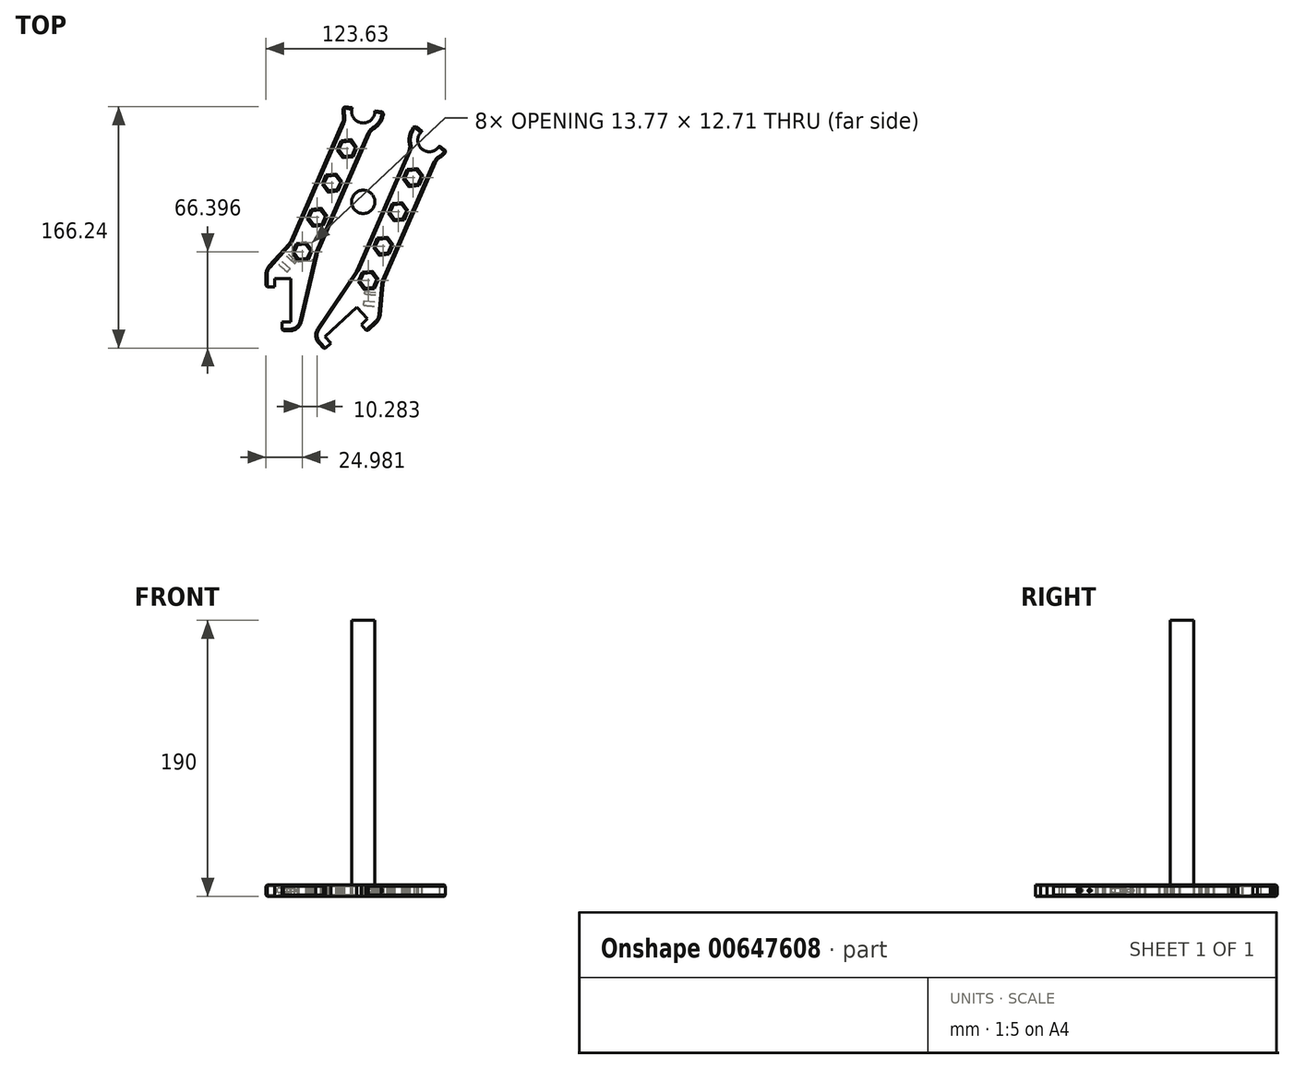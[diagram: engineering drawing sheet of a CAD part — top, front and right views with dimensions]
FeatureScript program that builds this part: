
annotation { "Feature Type Name" : "Feature", "Feature Type Description" : "" }
export const myFeature = defineFeature(function(context is Context, id is Id, definition is map)
    precondition{}
    {
        {
            var Q0;
            Q0=qCreatedBy(makeId("Top.planeOp"),FACE);
            var sketch = newSketch(context, id + "F0", { "sketchPlane" : qUnion([Q0])});
            skLineSegment(sketch, "E0.bottom", {"start": v(6, 6) * mm, "end": v(-17, 6) * mm, "construction": true});
            skLineSegment(sketch, "E0.top", {"start": v(6, -36) * mm, "end": v(-6, -36) * mm});
            skLineSegment(sketch, "E0.left", {"start": v(6, 6) * mm, "end": v(6, -36) * mm, "construction": true});
            skLineSegment(sketch, "E0.right", {"start": v(-17, 6) * mm, "end": v(-17, -6) * mm});
            skLineSegment(sketch, "E1", {"start": v(-17, -6) * mm, "end": v(-11, -6) * mm});
            skLineSegment(sketch, "E2", {"start": v(-11, -6) * mm, "end": v(-11, 0) * mm});
            skLineSegment(sketch, "E3", {"start": v(-11, 0) * mm, "end": v(0, 0) * mm});
            skLineSegment(sketch, "E4", {"start": v(0, 0) * mm, "end": v(0, -30) * mm});
            skLineSegment(sketch, "E5", {"start": v(0, -30) * mm, "end": v(-6, -30) * mm});
            skLineSegment(sketch, "E6", {"start": v(-6, -30) * mm, "end": v(-6, -36) * mm});
            skCircle(sketch, "E7", {"center": v(50, 115) * mm, "radius": 8 * mm});
            skCircle(sketch, "E8", {"center": v(50, 115) * mm, "radius": 14 * mm});
            skLineSegment(sketch, "E9", {"start": v(36.4, 118.32) * mm, "end": v(64, 114.57) * mm});
            skLineSegment(sketch, "E10", {"start": v(-17, 6) * mm, "end": v(0, 25.08) * mm});
            skLineSegment(sketch, "E11", {"start": v(0, 25.08) * mm, "end": v(36.92, 110) * mm});
            skLineSegment(sketch, "E12", {"start": v(18.34, 17.1) * mm, "end": v(6, -36) * mm});
            skLineSegment(sketch, "E13", {"start": v(18.34, 17.1) * mm, "end": v(55.26, 102.03) * mm});
            skLineSegment(sketch, "E14.0", {"start": v(0, 0) * mm, "end": v(50, 115) * mm, "construction": true});
            skLineSegment(sketch, "E15", {"start": v(0, 25.08) * mm, "end": v(18.34, 17.1) * mm, "construction": true});
            skCircle(sketch, "E16.cCircle", {"center": v(38.83, 89.3) * mm, "radius": 5.77 * mm, "construction": true});
            skLineSegment(sketch, "E16.0", {"start": v(36.53, 84.01) * mm, "end": v(33.1, 88.65) * mm});
            skLineSegment(sketch, "E16.1", {"start": v(33.1, 88.65) * mm, "end": v(35.4, 93.95) * mm});
            skLineSegment(sketch, "E16.2", {"start": v(35.4, 93.95) * mm, "end": v(41.13, 94.6) * mm});
            skLineSegment(sketch, "E16.3", {"start": v(41.13, 94.6) * mm, "end": v(44.57, 89.96) * mm});
            skLineSegment(sketch, "E16.4", {"start": v(44.57, 89.96) * mm, "end": v(42.26, 84.67) * mm});
            skLineSegment(sketch, "E16.5", {"start": v(42.26, 84.67) * mm, "end": v(36.53, 84.01) * mm});
            skCircle(sketch, "E17.cCircle", {"center": v(28.55, 65.66) * mm, "radius": 5.77 * mm, "construction": true});
            skLineSegment(sketch, "E17.0", {"start": v(26.24, 60.36) * mm, "end": v(22.81, 65) * mm});
            skLineSegment(sketch, "E17.1", {"start": v(22.81, 65) * mm, "end": v(25.11, 70.3) * mm});
            skLineSegment(sketch, "E17.2", {"start": v(25.11, 70.3) * mm, "end": v(30.85, 70.95) * mm});
            skLineSegment(sketch, "E17.3", {"start": v(30.85, 70.95) * mm, "end": v(34.28, 66.31) * mm});
            skLineSegment(sketch, "E17.4", {"start": v(34.28, 66.31) * mm, "end": v(31.98, 61.02) * mm});
            skLineSegment(sketch, "E17.5", {"start": v(31.98, 61.02) * mm, "end": v(26.24, 60.36) * mm});
            skCircle(sketch, "E18.cCircle", {"center": v(18.26, 42) * mm, "radius": 5.77 * mm, "construction": true});
            skLineSegment(sketch, "E18.0", {"start": v(15.96, 36.71) * mm, "end": v(12.53, 41.35) * mm});
            skLineSegment(sketch, "E18.1", {"start": v(12.53, 41.35) * mm, "end": v(14.83, 46.65) * mm});
            skLineSegment(sketch, "E18.2", {"start": v(14.83, 46.65) * mm, "end": v(20.57, 47.3) * mm});
            skLineSegment(sketch, "E18.3", {"start": v(20.57, 47.3) * mm, "end": v(24, 42.66) * mm});
            skLineSegment(sketch, "E18.4", {"start": v(24, 42.66) * mm, "end": v(21.7, 37.37) * mm});
            skLineSegment(sketch, "E18.5", {"start": v(21.7, 37.37) * mm, "end": v(15.96, 36.71) * mm});
            skCircle(sketch, "E19.cCircle", {"center": v(7.98, 18.36) * mm, "radius": 5.77 * mm, "construction": true});
            skLineSegment(sketch, "E19.0", {"start": v(5.68, 13.06) * mm, "end": v(2.24, 17.7) * mm});
            skLineSegment(sketch, "E19.1", {"start": v(2.24, 17.7) * mm, "end": v(4.55, 23) * mm});
            skLineSegment(sketch, "E19.2", {"start": v(4.55, 23) * mm, "end": v(10.28, 23.65) * mm});
            skLineSegment(sketch, "E19.3", {"start": v(10.28, 23.65) * mm, "end": v(13.72, 19) * mm});
            skLineSegment(sketch, "E19.4", {"start": v(13.72, 19) * mm, "end": v(11.42, 13.71) * mm});
            skLineSegment(sketch, "E19.5", {"start": v(11.42, 13.71) * mm, "end": v(5.68, 13.06) * mm});
            skLineSegment(sketch, "E20", {"start": v(41.13, 94.6) * mm, "end": v(46.81, 107.66) * mm, "construction": true});
            skLineSegment(sketch, "E21", {"start": v(30.85, 70.95) * mm, "end": v(36.53, 84.01) * mm, "construction": true});
            skLineSegment(sketch, "E22", {"start": v(20.57, 47.3) * mm, "end": v(26.24, 60.36) * mm, "construction": true});
            skLineSegment(sketch, "E23", {"start": v(10.28, 23.65) * mm, "end": v(15.96, 36.71) * mm, "construction": true});
            skLineSegment(sketch, "E24", {"start": v(5.68, 13.06) * mm, "end": v(0, 0) * mm, "construction": true});
            skSolve(sketch);
        }
        {
            var Q0;
            Q0=makeQuery(id+"F0.imprint","IMPRINT",FACE,{"disambiguationData":[TD([[makeQuery(id+"F0.imprint","IMPRINT",EDGE,{"derivedFrom":sQuery(id+"F0.wireOp",EDGE,"E0.top")}),-1.0]])]});
            var Q1;
            {var subQ0=sQuery(id+"F0.wireOp",EDGE,"E9");var subQ6=sQuery(id+"F0.wireOp",EDGE,"E7");var subQ7=makeQuery(id+"F0.imprint","INTERSECT",VERTEX,{"disambiguationData":[OD(0.0)],"derivedFrom":[subQ6,subQ0]});Q1=makeQuery(id+"F0.imprint","IMPRINT",FACE,{"disambiguationData":[TD([[makeQuery(id+"F0.imprint","IMPRINT",EDGE,{"disambiguationData":[TD([[subQ7,-1.0]])],"derivedFrom":subQ6}),-1.0]])]});}
            extrude(context, id + "F1", {"entities" : qUnion([Q0, Q1]), "depth" : 8 * mm, "offsetDistance" : 25 * mm});
        }
        {
            var Q0;
            Q0=makeQuery(id+"F1.opExtrude","SWEPT_EDGE",EDGE,{"disambiguationData":[OSD([sQuery(id+"F0.wireOp",EDGE,"E0.right"),sQuery(id+"F0.wireOp",EDGE,"E10")])]});
            var Q1;
            Q1=makeQuery(id+"F1.opExtrude","SWEPT_EDGE",EDGE,{"disambiguationData":[OSD([sQuery(id+"F0.wireOp",EDGE,"E10"),sQuery(id+"F0.wireOp",EDGE,"E11")])]});
            var Q2;
            Q2=makeQuery(id+"F1.opExtrude","SWEPT_EDGE",EDGE,{"disambiguationData":[OSD([sQuery(id+"F0.wireOp",EDGE,"E8"),sQuery(id+"F0.wireOp",EDGE,"E11")])]});
            var Q3;
            Q3=makeQuery(id+"F1.opExtrude","SWEPT_EDGE",EDGE,{"disambiguationData":[OSD([sQuery(id+"F0.wireOp",EDGE,"E8"),sQuery(id+"F0.wireOp",EDGE,"E13")])]});
            var Q4;
            Q4=makeQuery(id+"F1.opExtrude","SWEPT_EDGE",EDGE,{"disambiguationData":[OSD([sQuery(id+"F0.wireOp",EDGE,"E12"),sQuery(id+"F0.wireOp",EDGE,"E13")])]});
            var Q5;
            Q5=makeQuery(id+"F1.opExtrude","SWEPT_EDGE",EDGE,{"disambiguationData":[OSD([sQuery(id+"F0.wireOp",EDGE,"E0.top"),sQuery(id+"F0.wireOp",EDGE,"E12")])]});
            fillet(context, id + "F2", {"entities" : qUnion([Q0, Q1, Q2, Q3, Q4, Q5]), "radius" : 8 * mm, "tangentPropagation" : true, "allowEdgeOverflow" : false});
        }
        {
            var Q0;
            Q0=makeQuery(id+"F1.opExtrude","SWEPT_FACE",FACE,{"disambiguationData":[OSD([sQuery(id+"F0.wireOp",EDGE,"E10")])]});
            var sketch = newSketch(context, id + "F3", { "sketchPlane" : qUnion([Q0])});
            skCircle(sketch, "E25", {"center": v(-10.44, 4) * mm, "radius": 0.93 * mm});
            skCircle(sketch, "E26", {"center": v(-3.22, 4) * mm, "radius": 1.55 * mm});
            skLineSegment(sketch, "E27", {"start": v(3.78, 4) * mm, "end": v(-17.44, 4) * mm, "construction": true});
            skSolve(sketch);
        }
        {
            var Q0;
            Q0=makeQuery(id+"F3.imprint","IMPRINT",FACE,{"disambiguationData":[TD([[makeQuery(id+"F3.imprint","IMPRINT",EDGE,{"derivedFrom":sQuery(id+"F3.wireOp",EDGE,"E26")}),1.0]])]});
            var Q1;
            Q1=makeQuery(id+"F3.imprint","IMPRINT",FACE,{"disambiguationData":[TD([[makeQuery(id+"F3.imprint","IMPRINT",EDGE,{"derivedFrom":sQuery(id+"F3.wireOp",EDGE,"E25")}),1.0]])]});
            extrude(context, id + "F4", {"entities" : qUnion([Q0, Q1]), "operationType" : NewBodyOperationType.REMOVE, "oppositeDirection" : true, "depth" : 12 * mm, "offsetDistance" : 25 * mm});
        }
        {
            var Q0;
            {var subQ0=sQuery(id+"F0.wireOp",EDGE,"E9");Q0=makeQuery(id+"F1.opExtrude","CAP_EDGE",EDGE,{"disambiguationData":[OSD([subQ0]),TDD([makeQuery(id+"F0.imprint","IMPRINT",EDGE,{"disambiguationData":[TD([[makeQuery(id+"F0.imprint","INTERSECT",VERTEX,{"disambiguationData":[OD(0.0)],"derivedFrom":[sQuery(id+"F0.wireOp",EDGE,"E8"),subQ0]}),-1.0]])],"derivedFrom":subQ0})])],"isStart":false});}
            var Q1;
            {var subQ0=sQuery(id+"F0.wireOp",EDGE,"E9");Q1=makeQuery(id+"F1.opExtrude","CAP_EDGE",EDGE,{"disambiguationData":[OSD([subQ0]),TDD([makeQuery(id+"F0.imprint","IMPRINT",EDGE,{"disambiguationData":[TD([[makeQuery(id+"F0.imprint","INTERSECT",VERTEX,{"disambiguationData":[OD(1.0)],"derivedFrom":[sQuery(id+"F0.wireOp",EDGE,"E8"),subQ0]}),1.0]])],"derivedFrom":subQ0})])],"isStart":false});}
            var Q2;
            {var subQ0=sQuery(id+"F0.wireOp",EDGE,"E8");Q2=makeQuery(id+"F1.opExtrude","CAP_EDGE",EDGE,{"disambiguationData":[OSD([subQ0]),TDD([makeQuery(id+"F0.imprint","IMPRINT",EDGE,{"disambiguationData":[TD([[makeQuery(id+"F0.imprint","INTERSECT",VERTEX,{"disambiguationData":[OD(1.0)],"derivedFrom":[subQ0,sQuery(id+"F0.wireOp",EDGE,"E9")]}),1.0]])],"derivedFrom":subQ0})])],"isStart":false});}
            var Q3;
            {var subQ0=sQuery(id+"F0.wireOp",EDGE,"E8");Q3=makeQuery(id+"F1.opExtrude","CAP_EDGE",EDGE,{"disambiguationData":[OSD([subQ0]),TDD([makeQuery(id+"F0.imprint","IMPRINT",EDGE,{"disambiguationData":[TD([[makeQuery(id+"F0.imprint","INTERSECT",VERTEX,{"disambiguationData":[OD(0.0)],"derivedFrom":[subQ0,sQuery(id+"F0.wireOp",EDGE,"E9")]}),-1.0]])],"derivedFrom":subQ0})])],"isStart":false});}
            var Q4;
            Q4=makeQuery(id+"F1.opExtrude","CAP_EDGE",EDGE,{"disambiguationData":[OSD([sQuery(id+"F0.wireOp",EDGE,"E16.2")])],"isStart":false});
            var Q5;
            Q5=makeQuery(id+"F1.opExtrude","CAP_EDGE",EDGE,{"disambiguationData":[OSD([sQuery(id+"F0.wireOp",EDGE,"E16.3")])],"isStart":false});
            var Q6;
            Q6=makeQuery(id+"F1.opExtrude","CAP_EDGE",EDGE,{"disambiguationData":[OSD([sQuery(id+"F0.wireOp",EDGE,"E16.4")])],"isStart":false});
            var Q7;
            Q7=makeQuery(id+"F1.opExtrude","CAP_EDGE",EDGE,{"disambiguationData":[OSD([sQuery(id+"F0.wireOp",EDGE,"E16.5")])],"isStart":false});
            var Q8;
            Q8=makeQuery(id+"F1.opExtrude","CAP_EDGE",EDGE,{"disambiguationData":[OSD([sQuery(id+"F0.wireOp",EDGE,"E16.0")])],"isStart":false});
            var Q9;
            Q9=makeQuery(id+"F1.opExtrude","CAP_EDGE",EDGE,{"disambiguationData":[OSD([sQuery(id+"F0.wireOp",EDGE,"E16.1")])],"isStart":false});
            var Q10;
            Q10=makeQuery(id+"F1.opExtrude","CAP_EDGE",EDGE,{"disambiguationData":[OSD([sQuery(id+"F0.wireOp",EDGE,"E17.2")])],"isStart":false});
            var Q11;
            Q11=makeQuery(id+"F1.opExtrude","CAP_EDGE",EDGE,{"disambiguationData":[OSD([sQuery(id+"F0.wireOp",EDGE,"E17.3")])],"isStart":false});
            var Q12;
            Q12=makeQuery(id+"F1.opExtrude","CAP_EDGE",EDGE,{"disambiguationData":[OSD([sQuery(id+"F0.wireOp",EDGE,"E17.4")])],"isStart":false});
            var Q13;
            Q13=makeQuery(id+"F1.opExtrude","CAP_EDGE",EDGE,{"disambiguationData":[OSD([sQuery(id+"F0.wireOp",EDGE,"E17.5")])],"isStart":false});
            var Q14;
            Q14=makeQuery(id+"F1.opExtrude","CAP_EDGE",EDGE,{"disambiguationData":[OSD([sQuery(id+"F0.wireOp",EDGE,"E17.0")])],"isStart":false});
            var Q15;
            Q15=makeQuery(id+"F1.opExtrude","CAP_EDGE",EDGE,{"disambiguationData":[OSD([sQuery(id+"F0.wireOp",EDGE,"E17.1")])],"isStart":false});
            var Q16;
            Q16=makeQuery(id+"F1.opExtrude","CAP_EDGE",EDGE,{"disambiguationData":[OSD([sQuery(id+"F0.wireOp",EDGE,"E18.3")])],"isStart":false});
            var Q17;
            Q17=makeQuery(id+"F1.opExtrude","CAP_EDGE",EDGE,{"disambiguationData":[OSD([sQuery(id+"F0.wireOp",EDGE,"E18.4")])],"isStart":false});
            var Q18;
            Q18=makeQuery(id+"F1.opExtrude","CAP_EDGE",EDGE,{"disambiguationData":[OSD([sQuery(id+"F0.wireOp",EDGE,"E18.5")])],"isStart":false});
            var Q19;
            Q19=makeQuery(id+"F1.opExtrude","CAP_EDGE",EDGE,{"disambiguationData":[OSD([sQuery(id+"F0.wireOp",EDGE,"E18.0")])],"isStart":false});
            var Q20;
            Q20=makeQuery(id+"F1.opExtrude","CAP_EDGE",EDGE,{"disambiguationData":[OSD([sQuery(id+"F0.wireOp",EDGE,"E18.1")])],"isStart":false});
            var Q21;
            Q21=makeQuery(id+"F1.opExtrude","CAP_EDGE",EDGE,{"disambiguationData":[OSD([sQuery(id+"F0.wireOp",EDGE,"E18.2")])],"isStart":false});
            var Q22;
            Q22=makeQuery(id+"F1.opExtrude","CAP_EDGE",EDGE,{"disambiguationData":[OSD([sQuery(id+"F0.wireOp",EDGE,"E19.2")])],"isStart":false});
            var Q23;
            Q23=makeQuery(id+"F1.opExtrude","CAP_EDGE",EDGE,{"disambiguationData":[OSD([sQuery(id+"F0.wireOp",EDGE,"E19.3")])],"isStart":false});
            var Q24;
            Q24=makeQuery(id+"F1.opExtrude","CAP_EDGE",EDGE,{"disambiguationData":[OSD([sQuery(id+"F0.wireOp",EDGE,"E19.4")])],"isStart":false});
            var Q25;
            Q25=makeQuery(id+"F1.opExtrude","CAP_EDGE",EDGE,{"disambiguationData":[OSD([sQuery(id+"F0.wireOp",EDGE,"E19.5")])],"isStart":false});
            var Q26;
            Q26=makeQuery(id+"F1.opExtrude","CAP_EDGE",EDGE,{"disambiguationData":[OSD([sQuery(id+"F0.wireOp",EDGE,"E19.0")])],"isStart":false});
            var Q27;
            Q27=makeQuery(id+"F1.opExtrude","CAP_EDGE",EDGE,{"disambiguationData":[OSD([sQuery(id+"F0.wireOp",EDGE,"E19.1")])],"isStart":false});
            var Q28;
            {var subQ0=sQuery(id+"F0.wireOp",EDGE,"E9");Q28=makeQuery(id+"F1.opExtrude","CAP_EDGE",EDGE,{"disambiguationData":[OSD([subQ0]),TDD([makeQuery(id+"F0.imprint","IMPRINT",EDGE,{"disambiguationData":[TD([[makeQuery(id+"F0.imprint","INTERSECT",VERTEX,{"disambiguationData":[OD(0.0)],"derivedFrom":[sQuery(id+"F0.wireOp",EDGE,"E8"),subQ0]}),-1.0]])],"derivedFrom":subQ0})])],"isStart":true});}
            var Q29;
            {var subQ0=sQuery(id+"F0.wireOp",EDGE,"E9");Q29=makeQuery(id+"F1.opExtrude","CAP_EDGE",EDGE,{"disambiguationData":[OSD([subQ0]),TDD([makeQuery(id+"F0.imprint","IMPRINT",EDGE,{"disambiguationData":[TD([[makeQuery(id+"F0.imprint","INTERSECT",VERTEX,{"disambiguationData":[OD(1.0)],"derivedFrom":[sQuery(id+"F0.wireOp",EDGE,"E8"),subQ0]}),1.0]])],"derivedFrom":subQ0})])],"isStart":true});}
            var Q30;
            {var subQ0=sQuery(id+"F0.wireOp",EDGE,"E8");Q30=makeQuery(id+"F1.opExtrude","CAP_EDGE",EDGE,{"disambiguationData":[OSD([subQ0]),TDD([makeQuery(id+"F0.imprint","IMPRINT",EDGE,{"disambiguationData":[TD([[makeQuery(id+"F0.imprint","INTERSECT",VERTEX,{"disambiguationData":[OD(1.0)],"derivedFrom":[subQ0,sQuery(id+"F0.wireOp",EDGE,"E9")]}),1.0]])],"derivedFrom":subQ0})])],"isStart":true});}
            var Q31;
            {var subQ0=sQuery(id+"F0.wireOp",EDGE,"E8");Q31=makeQuery(id+"F1.opExtrude","CAP_EDGE",EDGE,{"disambiguationData":[OSD([subQ0]),TDD([makeQuery(id+"F0.imprint","IMPRINT",EDGE,{"disambiguationData":[TD([[makeQuery(id+"F0.imprint","INTERSECT",VERTEX,{"disambiguationData":[OD(0.0)],"derivedFrom":[subQ0,sQuery(id+"F0.wireOp",EDGE,"E9")]}),-1.0]])],"derivedFrom":subQ0})])],"isStart":true});}
            var Q32;
            Q32=makeQuery(id+"F1.opExtrude","CAP_EDGE",EDGE,{"disambiguationData":[OSD([sQuery(id+"F0.wireOp",EDGE,"E16.3")])],"isStart":true});
            var Q33;
            Q33=makeQuery(id+"F1.opExtrude","CAP_EDGE",EDGE,{"disambiguationData":[OSD([sQuery(id+"F0.wireOp",EDGE,"E16.2")])],"isStart":true});
            var Q34;
            Q34=makeQuery(id+"F1.opExtrude","CAP_EDGE",EDGE,{"disambiguationData":[OSD([sQuery(id+"F0.wireOp",EDGE,"E16.1")])],"isStart":true});
            var Q35;
            Q35=makeQuery(id+"F1.opExtrude","CAP_EDGE",EDGE,{"disambiguationData":[OSD([sQuery(id+"F0.wireOp",EDGE,"E16.0")])],"isStart":true});
            var Q36;
            Q36=makeQuery(id+"F1.opExtrude","CAP_EDGE",EDGE,{"disambiguationData":[OSD([sQuery(id+"F0.wireOp",EDGE,"E16.5")])],"isStart":true});
            var Q37;
            Q37=makeQuery(id+"F1.opExtrude","CAP_EDGE",EDGE,{"disambiguationData":[OSD([sQuery(id+"F0.wireOp",EDGE,"E16.4")])],"isStart":true});
            var Q38;
            Q38=makeQuery(id+"F1.opExtrude","CAP_EDGE",EDGE,{"disambiguationData":[OSD([sQuery(id+"F0.wireOp",EDGE,"E17.4")])],"isStart":true});
            var Q39;
            Q39=makeQuery(id+"F1.opExtrude","CAP_EDGE",EDGE,{"disambiguationData":[OSD([sQuery(id+"F0.wireOp",EDGE,"E17.3")])],"isStart":true});
            var Q40;
            Q40=makeQuery(id+"F1.opExtrude","CAP_EDGE",EDGE,{"disambiguationData":[OSD([sQuery(id+"F0.wireOp",EDGE,"E17.2")])],"isStart":true});
            var Q41;
            Q41=makeQuery(id+"F1.opExtrude","CAP_EDGE",EDGE,{"disambiguationData":[OSD([sQuery(id+"F0.wireOp",EDGE,"E17.1")])],"isStart":true});
            var Q42;
            Q42=makeQuery(id+"F1.opExtrude","CAP_EDGE",EDGE,{"disambiguationData":[OSD([sQuery(id+"F0.wireOp",EDGE,"E17.0")])],"isStart":true});
            var Q43;
            Q43=makeQuery(id+"F1.opExtrude","CAP_EDGE",EDGE,{"disambiguationData":[OSD([sQuery(id+"F0.wireOp",EDGE,"E17.5")])],"isStart":true});
            var Q44;
            Q44=makeQuery(id+"F1.opExtrude","CAP_EDGE",EDGE,{"disambiguationData":[OSD([sQuery(id+"F0.wireOp",EDGE,"E18.4")])],"isStart":true});
            var Q45;
            Q45=makeQuery(id+"F1.opExtrude","CAP_EDGE",EDGE,{"disambiguationData":[OSD([sQuery(id+"F0.wireOp",EDGE,"E18.3")])],"isStart":true});
            var Q46;
            Q46=makeQuery(id+"F1.opExtrude","CAP_EDGE",EDGE,{"disambiguationData":[OSD([sQuery(id+"F0.wireOp",EDGE,"E18.2")])],"isStart":true});
            var Q47;
            Q47=makeQuery(id+"F1.opExtrude","CAP_EDGE",EDGE,{"disambiguationData":[OSD([sQuery(id+"F0.wireOp",EDGE,"E18.1")])],"isStart":true});
            var Q48;
            Q48=makeQuery(id+"F1.opExtrude","CAP_EDGE",EDGE,{"disambiguationData":[OSD([sQuery(id+"F0.wireOp",EDGE,"E18.0")])],"isStart":true});
            var Q49;
            Q49=makeQuery(id+"F1.opExtrude","CAP_EDGE",EDGE,{"disambiguationData":[OSD([sQuery(id+"F0.wireOp",EDGE,"E18.5")])],"isStart":true});
            var Q50;
            Q50=makeQuery(id+"F1.opExtrude","CAP_EDGE",EDGE,{"disambiguationData":[OSD([sQuery(id+"F0.wireOp",EDGE,"E19.3")])],"isStart":true});
            var Q51;
            Q51=makeQuery(id+"F1.opExtrude","CAP_EDGE",EDGE,{"disambiguationData":[OSD([sQuery(id+"F0.wireOp",EDGE,"E19.4")])],"isStart":true});
            var Q52;
            Q52=makeQuery(id+"F1.opExtrude","CAP_EDGE",EDGE,{"disambiguationData":[OSD([sQuery(id+"F0.wireOp",EDGE,"E19.5")])],"isStart":true});
            var Q53;
            Q53=makeQuery(id+"F1.opExtrude","CAP_EDGE",EDGE,{"disambiguationData":[OSD([sQuery(id+"F0.wireOp",EDGE,"E19.0")])],"isStart":true});
            var Q54;
            Q54=makeQuery(id+"F1.opExtrude","CAP_EDGE",EDGE,{"disambiguationData":[OSD([sQuery(id+"F0.wireOp",EDGE,"E19.1")])],"isStart":true});
            var Q55;
            Q55=makeQuery(id+"F1.opExtrude","CAP_EDGE",EDGE,{"disambiguationData":[OSD([sQuery(id+"F0.wireOp",EDGE,"E19.2")])],"isStart":true});
            var Q56;
            Q56=makeQuery(id+"F4.boolean.opBoolean","COPY",EDGE,{"derivedFrom":makeQuery(id+"F4.opExtrude","CAP_EDGE",EDGE,{"disambiguationData":[OSD([sQuery(id+"F3.wireOp",EDGE,"E26")])],"isStart":true})});
            var Q57;
            Q57=makeQuery(id+"F4.boolean.opBoolean","COPY",EDGE,{"derivedFrom":makeQuery(id+"F4.opExtrude","CAP_EDGE",EDGE,{"disambiguationData":[OSD([sQuery(id+"F3.wireOp",EDGE,"E25")])],"isStart":true})});
            var Q58;
            Q58=makeQuery(id+"F1.opExtrude","SWEPT_EDGE",EDGE,{"disambiguationData":[OSD([sQuery(id+"F0.wireOp",EDGE,"E0.right"),sQuery(id+"F0.wireOp",EDGE,"E1")])]});
            var Q59;
            Q59=makeQuery(id+"F1.opExtrude","SWEPT_EDGE",EDGE,{"disambiguationData":[OSD([sQuery(id+"F0.wireOp",EDGE,"E0.top"),sQuery(id+"F0.wireOp",EDGE,"E6")])]});
            var Q60;
            {var subQ0=sQuery(id+"F0.wireOp",EDGE,"E9");var subQ1=sQuery(id+"F0.wireOp",EDGE,"E8");Q60=makeQuery(id+"F1.opExtrude","SWEPT_EDGE",EDGE,{"disambiguationData":[OSD([subQ1,subQ0]),TDD([makeQuery(id+"F0.imprint","INTERSECT",VERTEX,{"disambiguationData":[OD(1.0)],"derivedFrom":[subQ1,subQ0]})])]});}
            var Q61;
            {var subQ0=sQuery(id+"F0.wireOp",EDGE,"E9");var subQ1=sQuery(id+"F0.wireOp",EDGE,"E8");Q61=makeQuery(id+"F1.opExtrude","SWEPT_EDGE",EDGE,{"disambiguationData":[OSD([subQ1,subQ0]),TDD([makeQuery(id+"F0.imprint","INTERSECT",VERTEX,{"disambiguationData":[OD(0.0)],"derivedFrom":[subQ1,subQ0]})])]});}
            chamfer(context, id + "F5", {"entities" : qUnion([Q0, Q1, Q2, Q3, Q4, Q5, Q6, Q7, Q8, Q9, Q10, Q11, Q12, Q13, Q14, Q15, Q16, Q17, Q18, Q19, Q20, Q21, Q22, Q23, Q24, Q25, Q26, Q27, Q28, Q29, Q30, Q31, Q32, Q33, Q34, Q35, Q36, Q37, Q38, Q39, Q40, Q41, Q42, Q43, Q44, Q45, Q46, Q47, Q48, Q49, Q50, Q51, Q52, Q53, Q54, Q55, Q56, Q57, Q58, Q59, Q60, Q61]), "width" : 1 * mm, "tangentPropagation" : true});
        }
        {
            var Q0;
            Q0=makeQuery(id+"F1.opExtrude","SWEPT_FACE",FACE,{"disambiguationData":[OSD([sQuery(id+"F0.wireOp",EDGE,"E13")])]});
            cPlane(context, id + "F6", {"entities" : qUnion([Q0]), "cplaneType" : CPlaneType.OFFSET, "offset" : 14.8 * mm, "width" : 150 * mm, "height" : 150 * mm});
        }
        {
            var Q0;
            Q0=makeQuery(id+"F1.opExtrude","SWEPT_BODY",BODY,{"disambiguationData":[OSD([sQuery(id+"F0.wireOp",EDGE,"E0.top"),sQuery(id+"F0.wireOp",EDGE,"E0.right"),sQuery(id+"F0.wireOp",EDGE,"E1"),sQuery(id+"F0.wireOp",EDGE,"E2"),sQuery(id+"F0.wireOp",EDGE,"E3"),sQuery(id+"F0.wireOp",EDGE,"E4"),sQuery(id+"F0.wireOp",EDGE,"E5"),sQuery(id+"F0.wireOp",EDGE,"E6"),sQuery(id+"F0.wireOp",EDGE,"E7"),sQuery(id+"F0.wireOp",EDGE,"E8"),sQuery(id+"F0.wireOp",EDGE,"E9"),sQuery(id+"F0.wireOp",EDGE,"E10"),sQuery(id+"F0.wireOp",EDGE,"E11"),sQuery(id+"F0.wireOp",EDGE,"E12"),sQuery(id+"F0.wireOp",EDGE,"E13"),sQuery(id+"F0.wireOp",EDGE,"E16.0"),sQuery(id+"F0.wireOp",EDGE,"E16.1"),sQuery(id+"F0.wireOp",EDGE,"E16.2"),sQuery(id+"F0.wireOp",EDGE,"E16.3"),sQuery(id+"F0.wireOp",EDGE,"E16.4"),sQuery(id+"F0.wireOp",EDGE,"E16.5"),sQuery(id+"F0.wireOp",EDGE,"E17.0"),sQuery(id+"F0.wireOp",EDGE,"E17.1"),sQuery(id+"F0.wireOp",EDGE,"E17.2"),sQuery(id+"F0.wireOp",EDGE,"E17.3"),sQuery(id+"F0.wireOp",EDGE,"E17.4"),sQuery(id+"F0.wireOp",EDGE,"E17.5"),sQuery(id+"F0.wireOp",EDGE,"E18.0"),sQuery(id+"F0.wireOp",EDGE,"E18.1"),sQuery(id+"F0.wireOp",EDGE,"E18.2"),sQuery(id+"F0.wireOp",EDGE,"E18.3"),sQuery(id+"F0.wireOp",EDGE,"E18.4"),sQuery(id+"F0.wireOp",EDGE,"E18.5"),sQuery(id+"F0.wireOp",EDGE,"E19.0"),sQuery(id+"F0.wireOp",EDGE,"E19.1"),sQuery(id+"F0.wireOp",EDGE,"E19.2"),sQuery(id+"F0.wireOp",EDGE,"E19.3"),sQuery(id+"F0.wireOp",EDGE,"E19.4"),sQuery(id+"F0.wireOp",EDGE,"E19.5")])]});
            var Q1;
            Q1=qCreatedBy(id+"F6.planeOp",FACE);
            mirror(context, id + "F7", {"entities" : qUnion([Q0]), "mirrorPlane" : qUnion([Q1])});
        }
        {
            var Q0;
            Q0=qCreatedBy(makeId("Top.planeOp"),FACE);
            var sketch = newSketch(context, id + "F8", { "sketchPlane" : qUnion([Q0])});
            skCircle(sketch, "E28", {"center": v(49.95, 52.7) * mm, "radius": 8 * mm});
            skLineSegment(sketch, "E29", {"start": v(36.38, 58.6) * mm, "end": v(63.52, 46.8) * mm, "construction": true});
            skSolve(sketch);
        }
        {
            var Q0;
            Q0=makeQuery(id+"F8.imprint","IMPRINT",FACE,{"disambiguationData":[TD([[makeQuery(id+"F8.imprint","IMPRINT",EDGE,{"derivedFrom":sQuery(id+"F8.wireOp",EDGE,"E28")}),1.0]])]});
            extrude(context, id + "F9", {"entities" : qUnion([Q0]), "depth" : 190 * mm, "offsetDistance" : 25 * mm});
        }
    });
